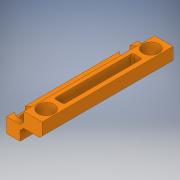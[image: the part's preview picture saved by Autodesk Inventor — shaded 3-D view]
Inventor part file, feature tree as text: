
AUTODESK INVENTOR PART (.ipt)
format: ipt  version: 2019 (Build 230136000, 136)  size: 220,160 bytes
history: native  units: in
note: dims shown in document units (in); Inventor stores cm internally (conversion verified against a paired STEP export)
features: sketch x7, extrude x5, hole x2, chamfer x2, fillet x1
ambient origin geometry x8: Origin, YZ Plane, XZ Plane, XY Plane, X Axis, Y Axis, Z Axis, Center Point
bodies: Solid1 (feature_tree)
feature tree (17):
  extrude  "Extrusion1"  Depth=0.65in
  hole  "Hole2"  [1 undecoded]
  hole  "Hole3"  [1 undecoded]
  extrude  "Extrusion2"  Depth=0.5in
  extrude  "Extrusion3"  Depth=0.35in
  fillet  "Fillet1"  Radius=0.5in
  chamfer  "Chamfer1"  Distance=0.565in
  extrude  "Extrusion4"  Depth=0.7in
  extrude  "Extrusion5"  Depth=0.5in
  chamfer  "Chamfer2"  Distance=1.0in
  sketch  "Sketch1"  dims[d0=0.565in d2=0.65in]
  sketch  "Sketch3"  dims[d6=0.7in d9=0.85in]
  sketch  "Sketch4"  dims[d10=5.0in d11=0.0in d25=0.5in]
  sketch  "Sketch5"  dims[d26=0.5in d27=0.25in]
  sketch  "Sketch6"  dims[d28=0.25in]
  sketch  "Sketch7"  dims[d29=0.375in d30=0.75in d31=0.375in d32=0.25in d33=0.5635in d34=1.0in d35=0.8108in d36=0.35in d37=0.5in]
  sketch  "Sketch8"  dims[d38=0.5in d39=0.625in d40=0.75in d41=0.375in d42=0.25in d43=0.5635in d44=1.0in d45=0.8108in d47=0.565in d48=0.7in d49=0.5in d50=1.0in d51=0.175in d52=1.0in d53=0.375in d54=1.0in d55=0.0in d57=0.15in d58=0.15in d59=1.0in d60=0.0in d61=0.075in d62=0.14in d63=0.125in d64=45.0deg d65=0.64in d66=0.64in d67=0.15in d68=0.0in d69=0.15in d70=0.0in d71=0.1in d72=0.125in d73=45.0deg d18=1.0in d19=1.0in d20=1.0in d21=0.15in d22=0.25in d23=0.375in d24=0.5635in]
note: 2 required parameter values undecoded (feature->parameter linkage not recoverable at this tier; creation-order binding heuristic only, values carry confidence <= 0.55)
